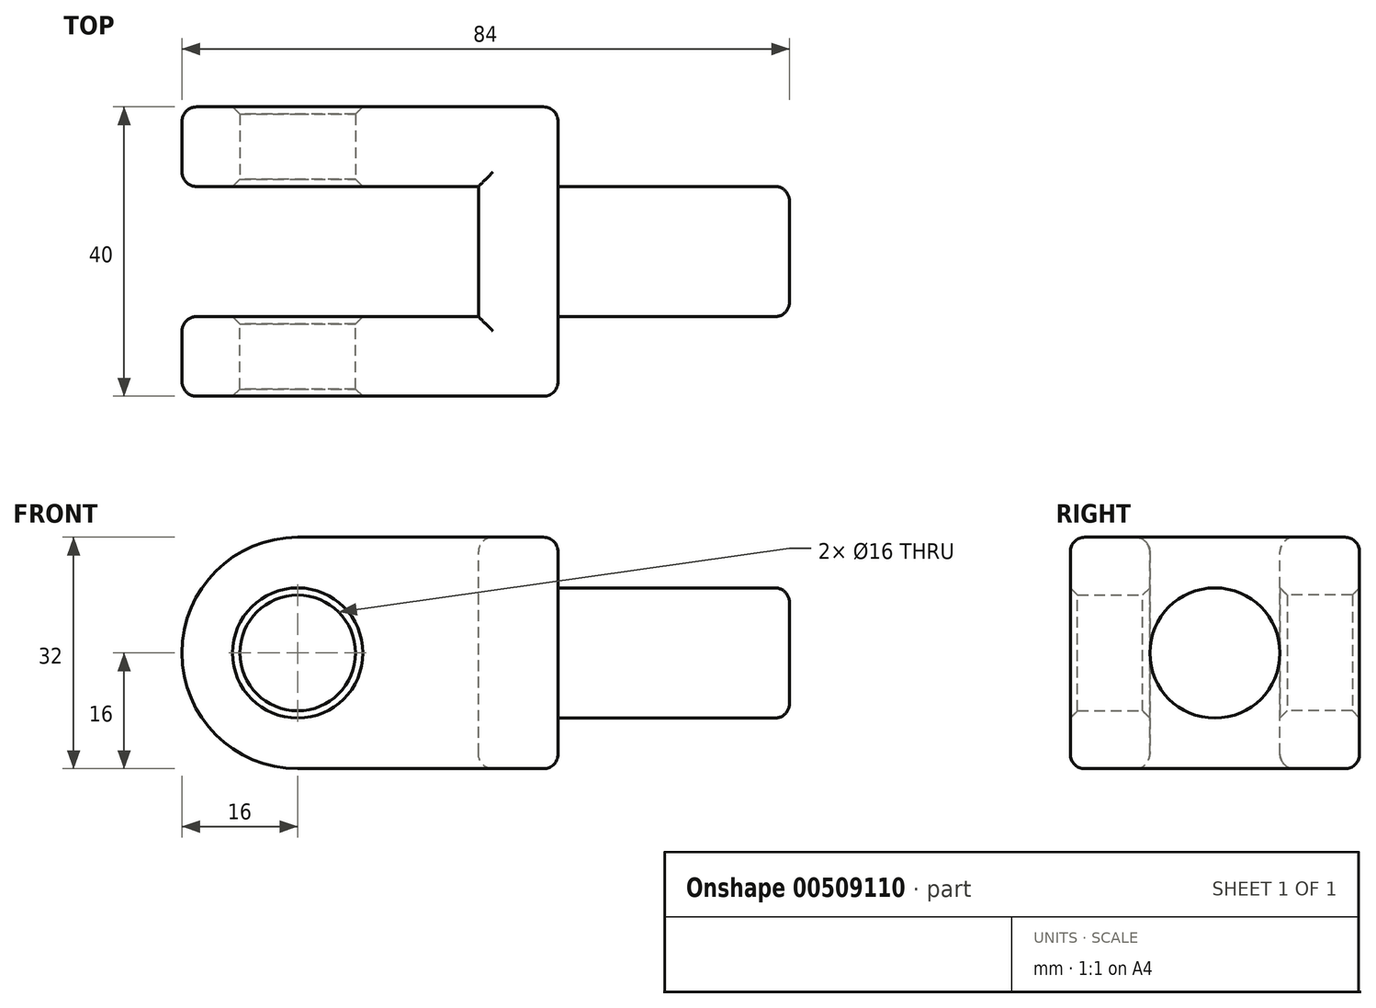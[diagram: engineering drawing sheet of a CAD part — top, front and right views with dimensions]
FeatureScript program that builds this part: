
annotation { "Feature Type Name" : "Feature", "Feature Type Description" : "" }
export const myFeature = defineFeature(function(context is Context, id is Id, definition is map)
    precondition{}
    {
        {
            var Q0;
            Q0=qCreatedBy(makeId("Front.planeOp"),FACE);
            var sketch = newSketch(context, id + "F0", { "sketchPlane" : qUnion([Q0])});
            skLineSegment(sketch, "E0", {"start": v(0, 0) * mm, "end": v(0, 32) * mm});
            skLineSegment(sketch, "E1", {"start": v(0, 32) * mm, "end": v(-36, 32) * mm});
            skLineSegment(sketch, "E2", {"start": v(0, 0) * mm, "end": v(-36, 0) * mm});
            skArc(sketch, "E3", {"start": v(-36, 32) * mm, "mid": v(-52, 16) * mm, "end": v(-36, 0) * mm});
            skCircle(sketch, "E4", {"center": v(-36, 16) * mm, "radius": 8 * mm});
            skLineSegment(sketch, "E5", {"start": v(-11, 0) * mm, "end": v(-11, 32) * mm});
            skSolve(sketch);
        }
        {
            var Q0;
            {var subQ0=sQuery(id+"F0.wireOp",EDGE,"E3");Q0=makeQuery(id+"F0.imprint","IMPRINT",FACE,{"disambiguationData":[TD([[makeQuery(id+"F0.imprint","IMPRINT",EDGE,{"derivedFrom":subQ0}),1.0]])]});}
            var Q1;
            {var subQ0=sQuery(id+"F0.wireOp",EDGE,"E0");Q1=makeQuery(id+"F0.imprint","IMPRINT",FACE,{"disambiguationData":[TD([[makeQuery(id+"F0.imprint","IMPRINT",EDGE,{"derivedFrom":subQ0}),1.0]])]});}
            extrude(context, id + "F1", {"entities" : qUnion([Q0, Q1]), "depth" : 11 * mm});
        }
        {
            var Q0;
            {var subQ0=sQuery(id+"F0.wireOp",EDGE,"E0");Q0=makeQuery(id+"F0.imprint","IMPRINT",FACE,{"disambiguationData":[TD([[makeQuery(id+"F0.imprint","IMPRINT",EDGE,{"derivedFrom":subQ0}),1.0]])]});}
            extrude(context, id + "F2", {"entities" : qUnion([Q0]), "operationType" : NewBodyOperationType.ADD, "oppositeDirection" : true, "depth" : 9 * mm});
        }
        {
            var Q0;
            Q0=makeQuery(id+"F1.opExtrude","SWEPT_BODY",BODY,{"disambiguationData":[OSD([sQuery(id+"F0.wireOp",EDGE,"E0"),sQuery(id+"F0.wireOp",EDGE,"E1"),sQuery(id+"F0.wireOp",EDGE,"E2"),sQuery(id+"F0.wireOp",EDGE,"E3"),sQuery(id+"F0.wireOp",EDGE,"E4")])]});
            var Q1;
            Q1=makeQuery(id+"F2.opExtrude","CAP_FACE",FACE,{"disambiguationData":[OSD([sQuery(id+"F0.wireOp",EDGE,"E0"),sQuery(id+"F0.wireOp",EDGE,"E1"),sQuery(id+"F0.wireOp",EDGE,"E2"),sQuery(id+"F0.wireOp",EDGE,"E5")])],"isStart":false});
            mirror(context, id + "F3", {"operationType" : NewBodyOperationType.ADD, "entities" : qUnion([Q0]), "mirrorPlane" : qUnion([Q1])});
        }
        {
            var Q0;
            {var subQ0=sQuery(id+"F0.wireOp",EDGE,"E0");var subQ1=makeQuery(id+"F2.boolean.opBoolean","MERGE",FACE,{"derivedFrom":[makeQuery(id+"F1.opExtrude","SWEPT_FACE",FACE,{"disambiguationData":[OSD([subQ0])]}),makeQuery(id+"F2.opExtrude","SWEPT_FACE",FACE,{"disambiguationData":[OSD([subQ0])]})]});Q0=makeQuery(id+"F3.boolean.opBoolean","MERGE",FACE,{"derivedFrom":[subQ1,makeQuery(id+"F3.opPattern","COPY",FACE,{"derivedFrom":subQ1,"instanceName":"1"})]});}
            var sketch = newSketch(context, id + "F4", { "sketchPlane" : qUnion([Q0])});
            skCircle(sketch, "E6", {"center": v(9, 16) * mm, "radius": 9 * mm});
            skSolve(sketch);
        }
        {
            var Q0;
            Q0=makeQuery(id+"F4.imprint","IMPRINT",FACE,{"disambiguationData":[TD([[makeQuery(id+"F4.imprint","IMPRINT",EDGE,{"derivedFrom":sQuery(id+"F4.wireOp",EDGE,"E6")}),1.0]])]});
            extrude(context, id + "F5", {"entities" : qUnion([Q0]), "operationType" : NewBodyOperationType.ADD, "depth" : 32 * mm});
        }
        {
            var Q0;
            Q0=makeQuery(id+"F1.opExtrude","SWEPT_FACE",FACE,{"disambiguationData":[OSD([sQuery(id+"F0.wireOp",EDGE,"E4")])]});
            var Q1;
            Q1=makeQuery(id+"F3.opPattern","COPY",FACE,{"derivedFrom":makeQuery(id+"F1.opExtrude","SWEPT_FACE",FACE,{"disambiguationData":[OSD([sQuery(id+"F0.wireOp",EDGE,"E4")])]}),"instanceName":"1"});
            chamfer(context, id + "F6", {"entities" : qUnion([Q0, Q1]), "width" : 1 * mm, "tangentPropagation" : true});
        }
        {
            var Q0;
            {var subQ0=sQuery(id+"F0.wireOp",EDGE,"E1");var subQ1=makeQuery(id+"F2.boolean.opBoolean","MERGE",FACE,{"derivedFrom":[makeQuery(id+"F1.opExtrude","SWEPT_FACE",FACE,{"disambiguationData":[OSD([subQ0])]}),makeQuery(id+"F2.opExtrude","SWEPT_FACE",FACE,{"disambiguationData":[OSD([subQ0])]})]});Q0=makeQuery(id+"F3.boolean.opBoolean","MERGE",FACE,{"derivedFrom":[subQ1,makeQuery(id+"F3.opPattern","COPY",FACE,{"derivedFrom":subQ1,"instanceName":"1"})]});}
            var Q1;
            {var subQ0=sQuery(id+"F0.wireOp",EDGE,"E2");var subQ1=makeQuery(id+"F2.boolean.opBoolean","MERGE",FACE,{"derivedFrom":[makeQuery(id+"F1.opExtrude","SWEPT_FACE",FACE,{"disambiguationData":[OSD([subQ0])]}),makeQuery(id+"F2.opExtrude","SWEPT_FACE",FACE,{"disambiguationData":[OSD([subQ0])]})]});Q1=makeQuery(id+"F3.boolean.opBoolean","MERGE",FACE,{"derivedFrom":[subQ1,makeQuery(id+"F3.opPattern","COPY",FACE,{"derivedFrom":subQ1,"instanceName":"1"})]});}
            var Q2;
            Q2=makeQuery(id+"F5.opExtrude","CAP_FACE",FACE,{"disambiguationData":[OSD([sQuery(id+"F4.wireOp",EDGE,"E6")])],"isStart":false});
            var Q3;
            Q3=makeQuery(id+"F3.opPattern","COPY",EDGE,{"derivedFrom":makeQuery(id+"F1.opExtrude","CAP_EDGE",EDGE,{"disambiguationData":[OSD([sQuery(id+"F0.wireOp",EDGE,"E0")])],"isStart":false}),"instanceName":"1"});
            var Q4;
            Q4=makeQuery(id+"F1.opExtrude","CAP_EDGE",EDGE,{"disambiguationData":[OSD([sQuery(id+"F0.wireOp",EDGE,"E0")])],"isStart":false});
            fillet(context, id + "F7", {"entities" : qUnion([Q0, Q1, Q2, Q3, Q4]), "radius" : 2 * mm, "tangentPropagation" : true, "allowEdgeOverflow" : false});
        }
    });
